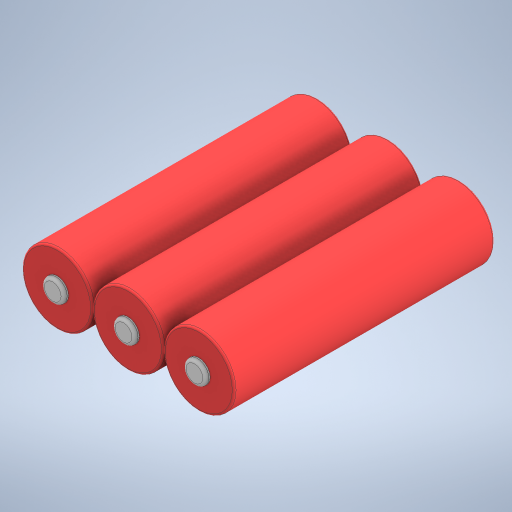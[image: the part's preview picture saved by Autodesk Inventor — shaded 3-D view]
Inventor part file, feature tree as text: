
AUTODESK INVENTOR PART (.ipt)
format: ipt  version: 2023.1 (Build 271208000, 208)  size: 316,928 bytes
history: native  units: mm
features: sketch x3, extrude x2, fillet x2, other x1, pattern_linear x1
ambient origin geometry x8: Origin, YZ Plane, XZ Plane, XY Plane, X Axis, Y Axis, Z Axis, Center Point
bodies: Body1 (feature_tree)
feature tree (9):
  other  "솔리드1"
  extrude  "돌출1"  Depth=18.6mm
  fillet  "모깎기1"  Radius=68.4mm
  extrude  "돌출3"  Depth=0.5mm
  fillet  "모깎기3"  Radius=6.0mm
  pattern_linear  "직사각형 패턴2"  Spacing1=1.15mm  [1 undecoded]
  sketch  "스케치1"
  sketch  "스케치4"
  sketch  "스케치5"
note: 1 required parameter value undecoded (feature->parameter linkage not recoverable at this tier; creation-order binding heuristic only, values carry confidence <= 0.55)
